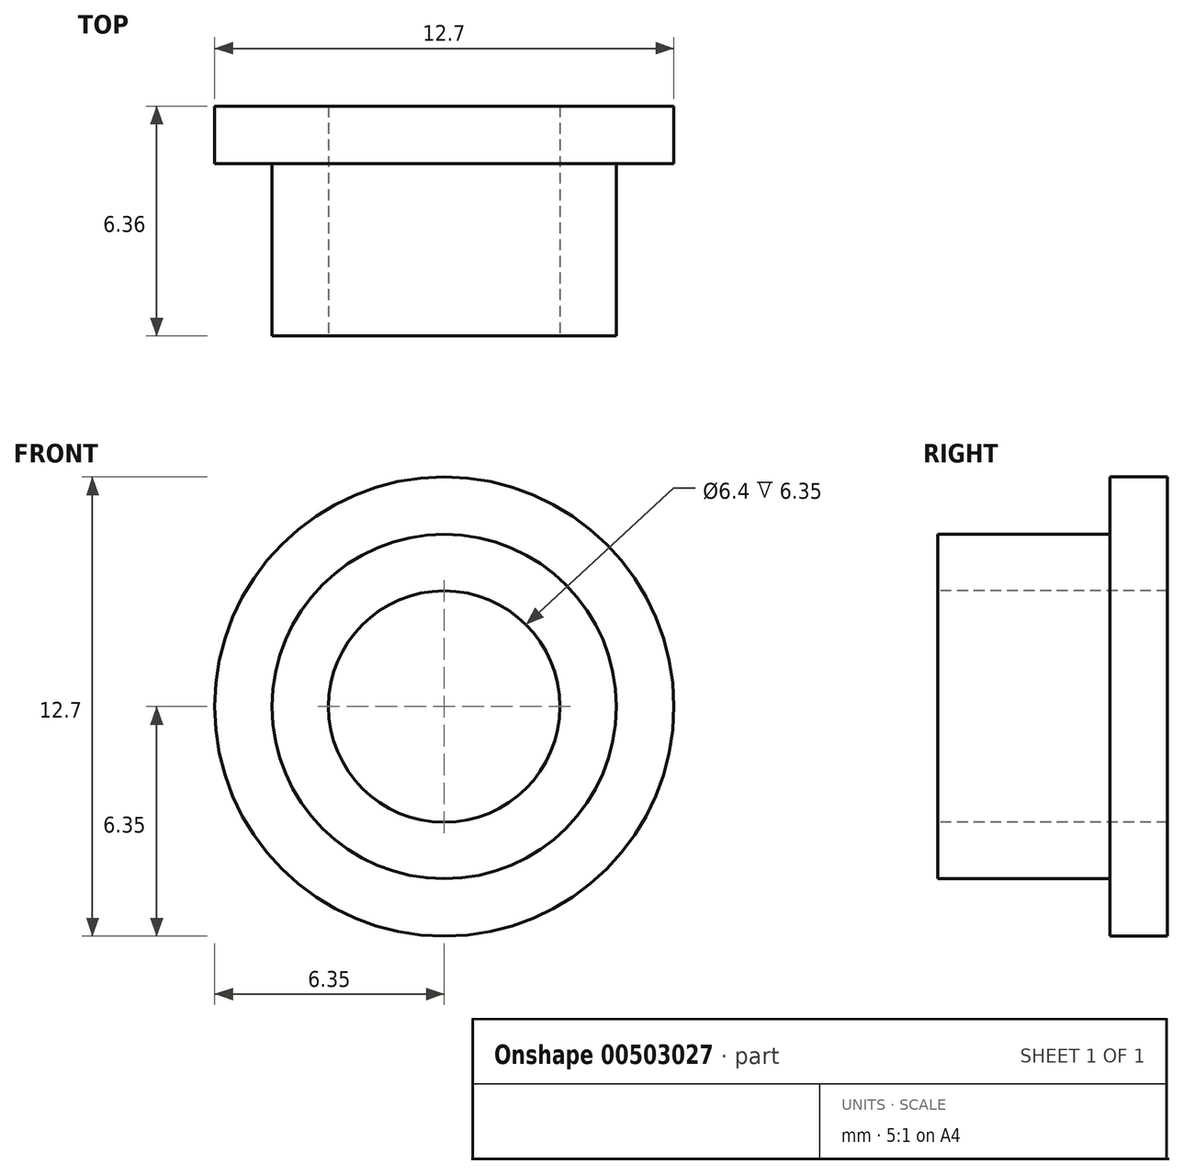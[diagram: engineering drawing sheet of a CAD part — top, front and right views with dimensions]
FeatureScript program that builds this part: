
annotation { "Feature Type Name" : "Feature", "Feature Type Description" : "" }
export const myFeature = defineFeature(function(context is Context, id is Id, definition is map)
    precondition{}
    {
        {
            var Q0;
            Q0=qCreatedBy(makeId("Right.planeOp"),FACE);
            var sketch = newSketch(context, id + "F0", { "sketchPlane" : qUnion([Q0])});
            skLineSegment(sketch, "E0", {"start": v(-3.17, 0) * mm, "end": v(3.17, 0) * mm, "construction": true});
            skLineSegment(sketch, "E1", {"start": v(-3.17, 3.2) * mm, "end": v(3.17, 3.2) * mm});
            skLineSegment(sketch, "E2", {"start": v(3.18, 3.2) * mm, "end": v(3.18, 6.35) * mm});
            skLineSegment(sketch, "E3", {"start": v(3.18, 6.35) * mm, "end": v(1.59, 6.35) * mm});
            skLineSegment(sketch, "E4", {"start": v(1.59, 6.35) * mm, "end": v(1.59, 4.76) * mm});
            skLineSegment(sketch, "E5", {"start": v(1.59, 4.76) * mm, "end": v(-3.17, 4.76) * mm});
            skLineSegment(sketch, "E6", {"start": v(-3.17, 4.76) * mm, "end": v(-3.17, 3.2) * mm});
            skSolve(sketch);
        }
        {
            var Q0;
            Q0=makeQuery(id+"F0.imprint","IMPRINT",FACE,{"disambiguationData":[TD([[makeQuery(id+"F0.imprint","IMPRINT",EDGE,{"derivedFrom":sQuery(id+"F0.wireOp",EDGE,"E1")}),1.0]])]});
            var Q1;
            Q1=sQuery(id+"F0.wireOp",EDGE,"E0");
            revolve(context, id + "F1", {"entities" : qUnion([Q0]), "axis" : qUnion([Q1]), "revolveType" : RevolveType.FULL});
        }
    });
